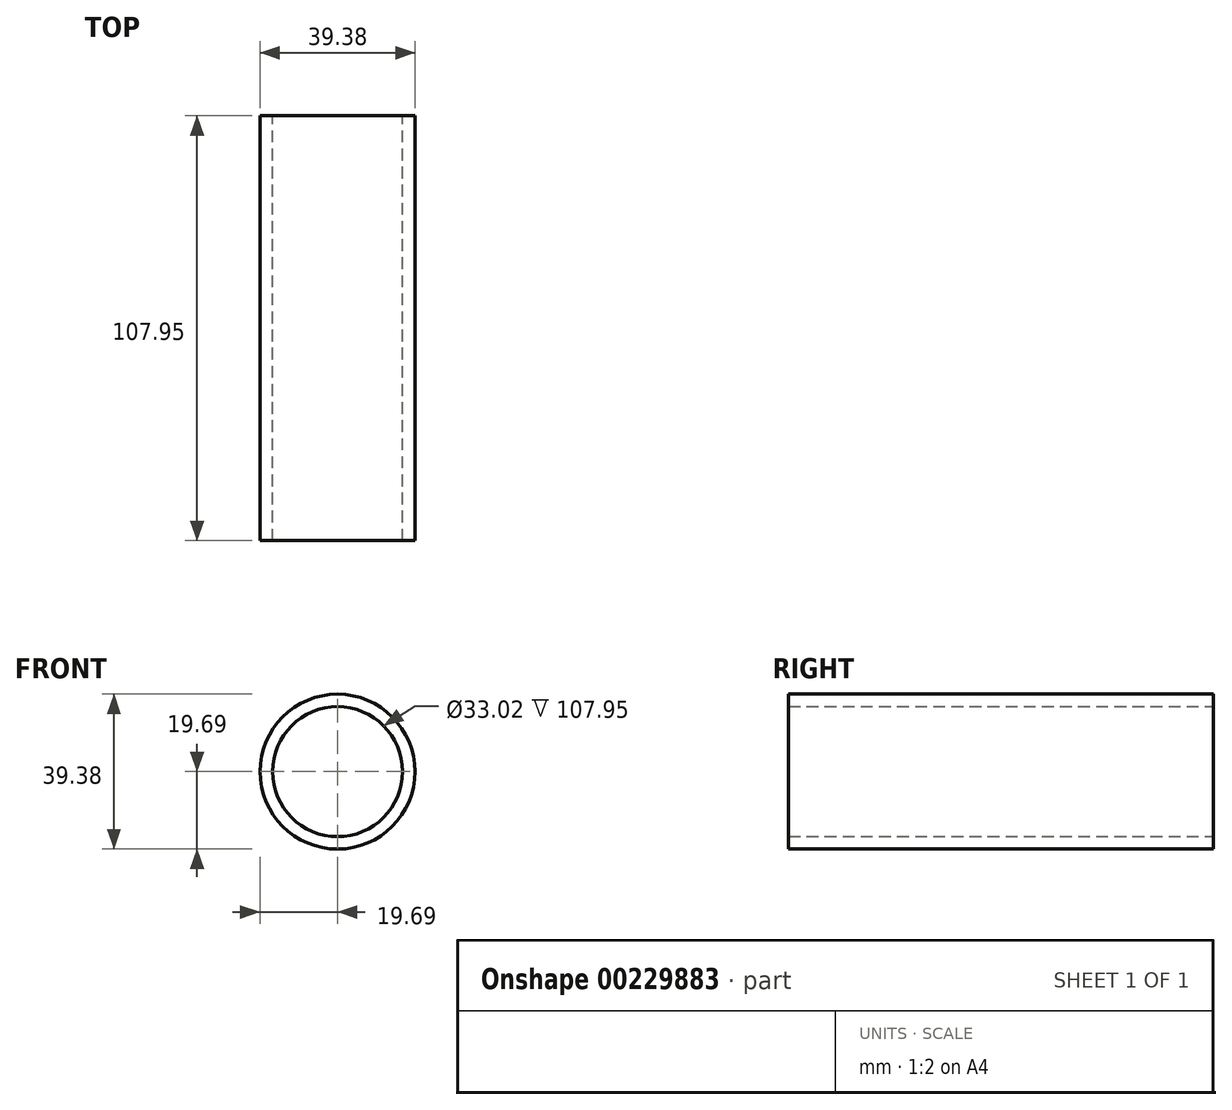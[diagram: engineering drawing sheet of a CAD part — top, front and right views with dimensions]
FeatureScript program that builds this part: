
annotation { "Feature Type Name" : "Feature", "Feature Type Description" : "" }
export const myFeature = defineFeature(function(context is Context, id is Id, definition is map)
    precondition{}
    {
        {
            var Q0;
            Q0=qCreatedBy(makeId("Front.planeOp"),FACE);
            var sketch = newSketch(context, id + "F0", { "sketchPlane" : qUnion([Q0])});
            skCircle(sketch, "E0", {"center": v(0, 0) * mm, "radius": 16.51 * mm});
            skCircle(sketch, "E1", {"center": v(0, 0) * mm, "radius": 19.69 * mm});
            skSolve(sketch);
        }
        {
            var Q0;
            Q0 = qSketchRegion(id + "F0", true);
            extrude(context, id + "F1", {"entities" : qUnion([Q0]), "depth" : 107.95 * mm});
        }
    });
